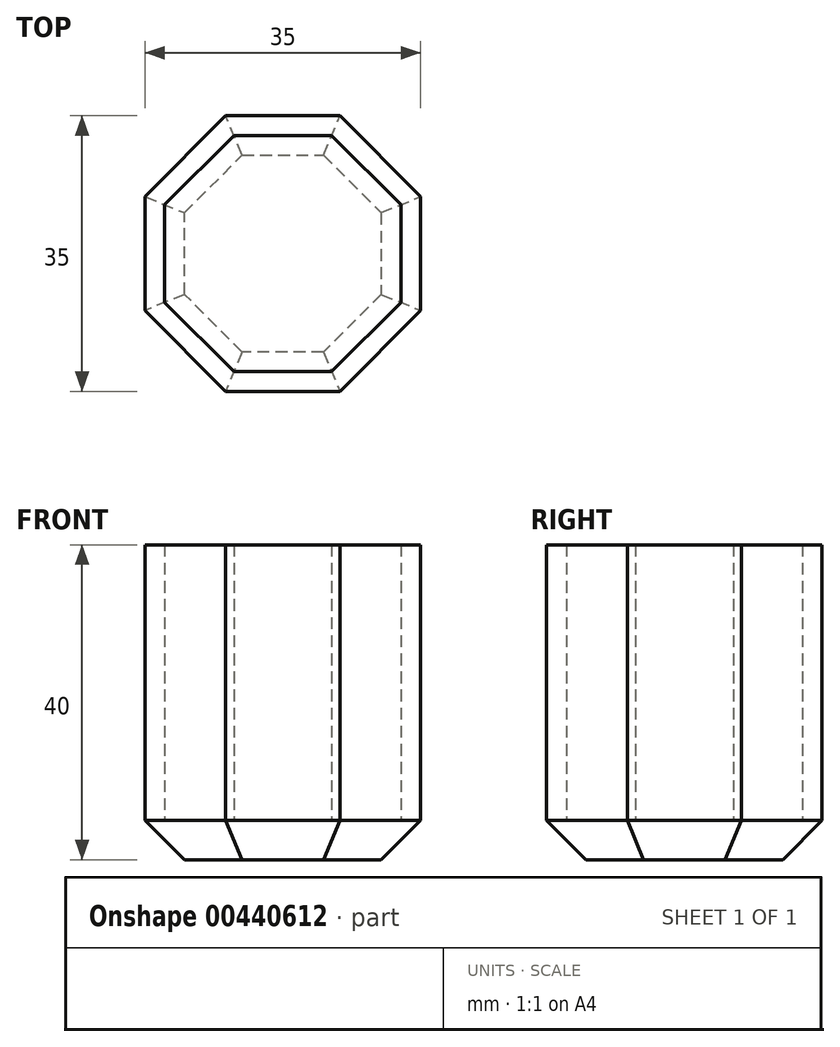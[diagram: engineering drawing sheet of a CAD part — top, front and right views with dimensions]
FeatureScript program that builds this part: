
annotation { "Feature Type Name" : "Feature", "Feature Type Description" : "" }
export const myFeature = defineFeature(function(context is Context, id is Id, definition is map)
    precondition{}
    {
        {
            var Q0;
            Q0=qCreatedBy(makeId("Top.planeOp"),FACE);
            var sketch = newSketch(context, id + "F0", { "sketchPlane" : qUnion([Q0])});
            skCircle(sketch, "E0.cCircle", {"center": v(0, 0) * mm, "radius": 17.5 * mm, "construction": true});
            skLineSegment(sketch, "E0.0", {"start": v(-17.5, -7.25) * mm, "end": v(-17.5, 7.25) * mm});
            skLineSegment(sketch, "E0.1", {"start": v(-17.5, 7.25) * mm, "end": v(-7.25, 17.5) * mm});
            skLineSegment(sketch, "E0.2", {"start": v(-7.25, 17.5) * mm, "end": v(7.25, 17.5) * mm});
            skLineSegment(sketch, "E0.3", {"start": v(7.25, 17.5) * mm, "end": v(17.5, 7.25) * mm});
            skLineSegment(sketch, "E0.4", {"start": v(17.5, 7.25) * mm, "end": v(17.5, -7.25) * mm});
            skLineSegment(sketch, "E0.5", {"start": v(17.5, -7.25) * mm, "end": v(7.25, -17.5) * mm});
            skLineSegment(sketch, "E0.6", {"start": v(7.25, -17.5) * mm, "end": v(-7.25, -17.5) * mm});
            skLineSegment(sketch, "E0.7", {"start": v(-7.25, -17.5) * mm, "end": v(-17.5, -7.25) * mm});
            skPoint(sketch, "E0.0.midPoint", {"position": v(-17.5, 0) * mm});
            skCircle(sketch, "E1.cCircle", {"center": v(0, 0) * mm, "radius": 15 * mm, "construction": true});
            skLineSegment(sketch, "E1.0", {"start": v(-15, -6.21) * mm, "end": v(-15, 6.21) * mm});
            skLineSegment(sketch, "E1.1", {"start": v(-15, 6.21) * mm, "end": v(-6.21, 15) * mm});
            skLineSegment(sketch, "E1.2", {"start": v(-6.21, 15) * mm, "end": v(6.21, 15) * mm});
            skLineSegment(sketch, "E1.3", {"start": v(6.21, 15) * mm, "end": v(15, 6.21) * mm});
            skLineSegment(sketch, "E1.4", {"start": v(15, 6.21) * mm, "end": v(15, -6.21) * mm});
            skLineSegment(sketch, "E1.5", {"start": v(15, -6.21) * mm, "end": v(6.21, -15) * mm});
            skLineSegment(sketch, "E1.6", {"start": v(6.21, -15) * mm, "end": v(-6.21, -15) * mm});
            skLineSegment(sketch, "E1.7", {"start": v(-6.21, -15) * mm, "end": v(-15, -6.21) * mm});
            skPoint(sketch, "E1.0.midPoint", {"position": v(-15, 0) * mm});
            skSolve(sketch);
        }
        {
            var Q0;
            Q0=makeQuery(id+"F0.imprint","IMPRINT",FACE,{"disambiguationData":[TD([[makeQuery(id+"F0.imprint","IMPRINT",EDGE,{"derivedFrom":sQuery(id+"F0.wireOp",EDGE,"E0.0")}),-1.0]])]});
            extrude(context, id + "F1", {"entities" : qUnion([Q0]), "depth" : 40 * mm});
        }
        {
            var Q0;
            Q0=makeQuery(id+"F0.imprint","IMPRINT",FACE,{"disambiguationData":[TD([[makeQuery(id+"F0.imprint","IMPRINT",EDGE,{"derivedFrom":sQuery(id+"F0.wireOp",EDGE,"E1.0")}),-1.0]])]});
            extrude(context, id + "F2", {"entities" : qUnion([Q0]), "operationType" : NewBodyOperationType.ADD, "depth" : 5 * mm});
        }
        {
            var Q0;
            Q0=makeQuery(id+"F1.opExtrude","CAP_EDGE",EDGE,{"disambiguationData":[OSD([sQuery(id+"F0.wireOp",EDGE,"E0.5")])],"isStart":true});
            var Q1;
            Q1=makeQuery(id+"F1.opExtrude","CAP_EDGE",EDGE,{"disambiguationData":[OSD([sQuery(id+"F0.wireOp",EDGE,"E0.6")])],"isStart":true});
            var Q2;
            Q2=makeQuery(id+"F1.opExtrude","CAP_EDGE",EDGE,{"disambiguationData":[OSD([sQuery(id+"F0.wireOp",EDGE,"E0.4")])],"isStart":true});
            var Q3;
            Q3=makeQuery(id+"F1.opExtrude","CAP_EDGE",EDGE,{"disambiguationData":[OSD([sQuery(id+"F0.wireOp",EDGE,"E0.3")])],"isStart":true});
            var Q4;
            Q4=makeQuery(id+"F1.opExtrude","CAP_EDGE",EDGE,{"disambiguationData":[OSD([sQuery(id+"F0.wireOp",EDGE,"E0.2")])],"isStart":true});
            var Q5;
            Q5=makeQuery(id+"F1.opExtrude","CAP_EDGE",EDGE,{"disambiguationData":[OSD([sQuery(id+"F0.wireOp",EDGE,"E0.1")])],"isStart":true});
            var Q6;
            Q6=makeQuery(id+"F1.opExtrude","CAP_EDGE",EDGE,{"disambiguationData":[OSD([sQuery(id+"F0.wireOp",EDGE,"E0.0")])],"isStart":true});
            var Q7;
            Q7=makeQuery(id+"F1.opExtrude","CAP_EDGE",EDGE,{"disambiguationData":[OSD([sQuery(id+"F0.wireOp",EDGE,"E0.7")])],"isStart":true});
            chamfer(context, id + "F3", {"entities" : qUnion([Q0, Q1, Q2, Q3, Q4, Q5, Q6, Q7]), "width" : 5 * mm, "tangentPropagation" : true});
        }
    });
